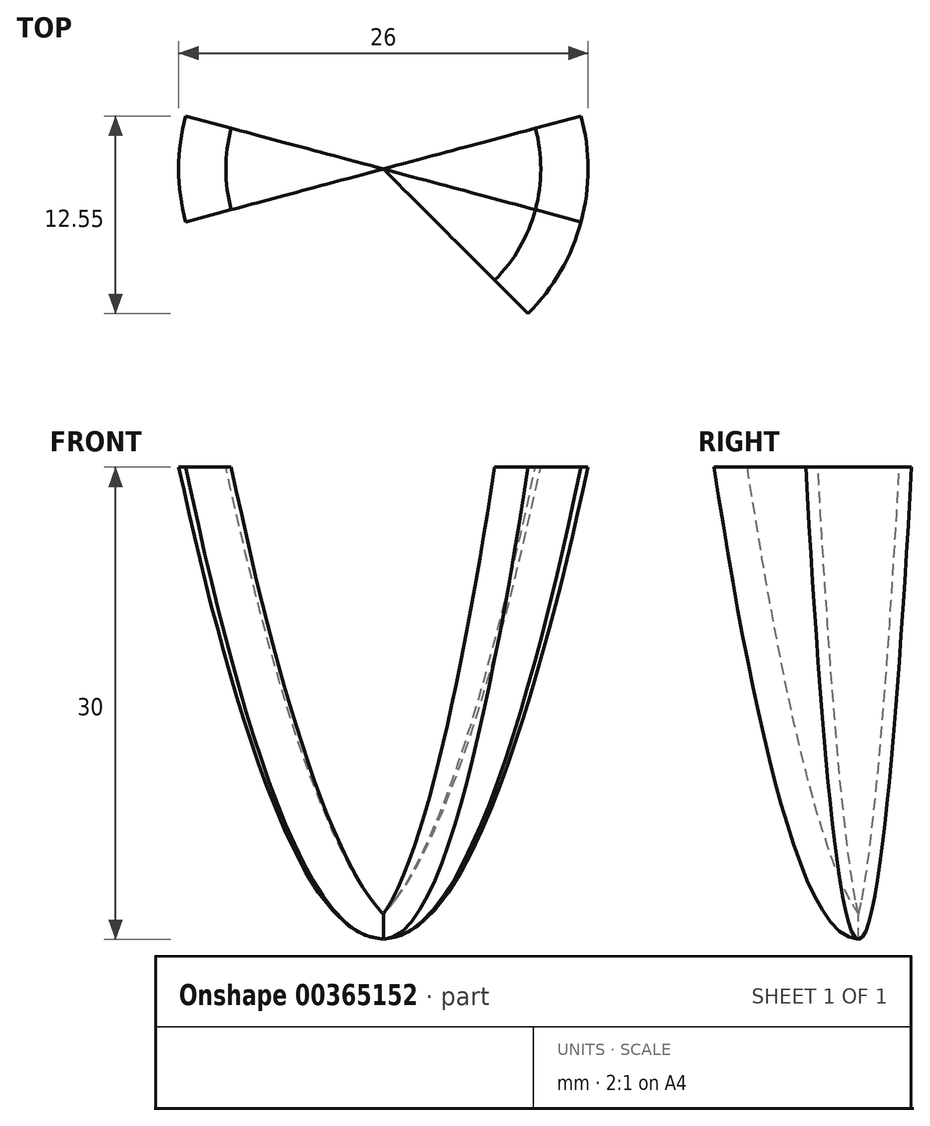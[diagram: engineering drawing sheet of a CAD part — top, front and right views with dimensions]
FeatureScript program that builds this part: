
annotation { "Feature Type Name" : "Feature", "Feature Type Description" : "" }
export const myFeature = defineFeature(function(context is Context, id is Id, definition is map)
    precondition{}
    {
        {
            var Q0;
            Q0=qCreatedBy(makeId("Front.planeOp"),FACE);
            var sketch = newSketch(context, id + "F0", { "sketchPlane" : qUnion([Q0])});
            skLineSegment(sketch, "E0", {"start": v(0, 0) * mm, "end": v(-13, 0) * mm});
            skLineSegment(sketch, "E1", {"start": v(-13, 0) * mm, "end": v(-13, -32) * mm, "construction": true});
            skLineSegment(sketch, "E2", {"start": v(-13, -32) * mm, "end": v(0, -32) * mm, "construction": true});
            skLineSegment(sketch, "E3.0", {"start": v(0, -2) * mm, "end": v(-13, -2) * mm});
            skLineSegment(sketch, "E4", {"start": v(0, 0) * mm, "end": v(-9, 0) * mm});
            skLineSegment(sketch, "E5", {"start": v(0, 0) * mm, "end": v(-3.25, 0) * mm});
            skLineSegment(sketch, "E6.MirrorCS", {"start": v(0, -2) * mm, "end": v(13, -2) * mm, "construction": true});
            skLineSegment(sketch, "E7.4", {"start": v(-5.38, 13) * mm, "end": v(5.38, 13) * mm});
            skPoint(sketch, "E7.0.midPoint", {"position": v(0, -32) * mm});
            skLineSegment(sketch, "E8.MirrorCS", {"start": v(13, 0) * mm, "end": v(13, -32) * mm, "construction": true});
            skLineSegment(sketch, "E9.MirrorCS", {"start": v(13, -32) * mm, "end": v(0, -32) * mm, "construction": true});
            skLineSegment(sketch, "E10.0", {"start": v(-8, 0) * mm, "end": v(-8, -32) * mm, "construction": true});
            skLineSegment(sketch, "E11.0", {"start": v(-12, 0) * mm, "end": v(-12, -32) * mm, "construction": true});
            skLineSegment(sketch, "E12.0", {"start": v(-11, 0) * mm, "end": v(-11, -32) * mm, "construction": true});
            skLineSegment(sketch, "E13.0", {"start": v(-10, 0) * mm, "end": v(-10, -32) * mm, "construction": true});
            skLineSegment(sketch, "E14.0", {"start": v(-9, 0) * mm, "end": v(-9, -32) * mm, "construction": true});
            skLineSegment(sketch, "E15.0", {"start": v(-3, 0) * mm, "end": v(-3, -32) * mm, "construction": true});
            skLineSegment(sketch, "E16.0", {"start": v(-4, 0) * mm, "end": v(-4, -32) * mm, "construction": true});
            skLineSegment(sketch, "E17.0", {"start": v(-5, 0) * mm, "end": v(-5, -32) * mm, "construction": true});
            skLineSegment(sketch, "E18.0", {"start": v(-6, 0) * mm, "end": v(-6, -32) * mm, "construction": true});
            skLineSegment(sketch, "E19.0", {"start": v(-7, 0) * mm, "end": v(-7, -32) * mm, "construction": true});
            skLineSegment(sketch, "E20.0", {"start": v(-2, 0) * mm, "end": v(-2, -32) * mm, "construction": true});
            skLineSegment(sketch, "E21.0", {"start": v(-1, 0) * mm, "end": v(-1, -32) * mm, "construction": true});
            skLineSegment(sketch, "E22.0", {"start": v(0, -116.4) * mm, "end": v(-13, -116.4) * mm, "construction": true});
            skLineSegment(sketch, "E23.0", {"start": v(0, -31.8) * mm, "end": v(-13, -31.8) * mm, "construction": true});
            skLineSegment(sketch, "E24.0", {"start": v(0, -31.3) * mm, "end": v(-13, -31.3) * mm, "construction": true});
            skLineSegment(sketch, "E25.0", {"start": v(0, -30.4) * mm, "end": v(-13, -30.4) * mm, "construction": true});
            skLineSegment(sketch, "E26.0", {"start": v(0, -29.2) * mm, "end": v(-13, -29.2) * mm, "construction": true});
            skLineSegment(sketch, "E27.0", {"start": v(0, -27.6) * mm, "end": v(-13, -27.6) * mm, "construction": true});
            skLineSegment(sketch, "E28.0", {"start": v(0, -25.6) * mm, "end": v(-13, -25.6) * mm, "construction": true});
            skLineSegment(sketch, "E29.0", {"start": v(0, -23.3) * mm, "end": v(-13, -23.3) * mm, "construction": true});
            skLineSegment(sketch, "E30.0", {"start": v(0, -20.6) * mm, "end": v(-13, -20.6) * mm, "construction": true});
            skLineSegment(sketch, "E31.0", {"start": v(0, -17.6) * mm, "end": v(-13, -17.6) * mm, "construction": true});
            skLineSegment(sketch, "E32.0", {"start": v(0, -14.2) * mm, "end": v(-13, -14.2) * mm, "construction": true});
            skLineSegment(sketch, "E33.0", {"start": v(0, -10.5) * mm, "end": v(-13, -10.5) * mm, "construction": true});
            skLineSegment(sketch, "E34.0", {"start": v(0, -6.4) * mm, "end": v(-13, -6.4) * mm, "construction": true});
            skFitSpline(sketch, "E35", {"points": [v(0, -32) * mm, v(-1, -31.8) * mm, v(-2, -31.3) * mm, v(-3, -30.4) * mm, v(-4, -29.2) * mm, v(-5, -27.6) * mm, v(-6, -25.6) * mm, v(-7, -23.3) * mm, v(-8, -20.6) * mm, v(-9, -17.6) * mm, v(-10, -14.2) * mm, v(-11, -10.5) * mm, v(-12, -6.4) * mm, v(-13, -2) * mm], "startDerivative": vector(-20.36, 2.94) * mm, "endDerivative": vector(-9.56, 42.59) * mm});
            skFitSpline(sketch, "E36", {"points": [v(0, -30.4) * mm, v(-1, -29.2) * mm, v(-2, -27.6) * mm, v(-3, -25.6) * mm, v(-4, -23.3) * mm, v(-5, -20.6) * mm, v(-6, -17.6) * mm, v(-7, -14.2) * mm, v(-8, -10.5) * mm, v(-9, -6.4) * mm, v(-10, -2) * mm], "startDerivative": vector(-14.02, 15.78) * mm, "endDerivative": vector(-8.05, 35.86) * mm});
            skArc(sketch, "E37.filletArc", {"start": v(-0.78, -29.48) * mm, "mid": v(-0.44, -29.76) * mm, "end": v(0, -29.86) * mm});
            skLineSegment(sketch, "E38", {"start": v(0, 0) * mm, "end": v(13, 0) * mm, "construction": true});
            skLineSegment(sketch, "E39", {"start": v(-13, -2) * mm, "end": v(-13, 0) * mm});
            skLineSegment(sketch, "E40", {"start": v(0, -32) * mm, "end": v(0, -29.86) * mm});
            skSolve(sketch);
        }
        {
            var Q0;
            {var subQ1=sQuery(id+"F0.wireOp",EDGE,"E35");Q0=makeQuery(id+"F0.imprint","IMPRINT",FACE,{"disambiguationData":[TD([[makeQuery(id+"F0.imprint","IMPRINT",EDGE,{"derivedFrom":subQ1}),-1.0]])]});}
            var Q1;
            Q1=sQuery(id+"F0.wireOp",EDGE,"E40");
            revolve(context, id + "F1", {"entities" : qUnion([Q0]), "axis" : qUnion([Q1]), "revolveType" : RevolveType.ONE_DIRECTION, "angle" : 15 * degree});
        }
        {
            var Q0;
            Q0=makeQuery(id+"F1.opRevolve","SWEPT_BODY",BODY,{"disambiguationData":[OSD([sQuery(id+"F0.wireOp",EDGE,"E3.0"),sQuery(id+"F0.wireOp",EDGE,"E35"),sQuery(id+"F0.wireOp",EDGE,"E36"),sQuery(id+"F0.wireOp",EDGE,"E37.filletArc"),sQuery(id+"F0.wireOp",EDGE,"E40")])]});
            var Q1;
            Q1=qCreatedBy(makeId("Right.planeOp"),FACE);
            mirror(context, id + "F2", {"entities" : qUnion([Q0]), "mirrorPlane" : qUnion([Q1])});
        }
        {
            var Q0;
            Q0=makeQuery(id+"F2.opPattern","COPY",BODY,{"derivedFrom":makeQuery(id+"F1.opRevolve","SWEPT_BODY",BODY,{"disambiguationData":[OSD([sQuery(id+"F0.wireOp",EDGE,"E3.0"),sQuery(id+"F0.wireOp",EDGE,"E35"),sQuery(id+"F0.wireOp",EDGE,"E36"),sQuery(id+"F0.wireOp",EDGE,"E37.filletArc"),sQuery(id+"F0.wireOp",EDGE,"E40")])]}),"instanceName":"1"});
            var Q1;
            Q1=makeQuery(id+"F2.opPattern","COPY",FACE,{"derivedFrom":makeQuery(id+"F1.opRevolve","CAP_FACE",FACE,{"disambiguationData":[OSD([sQuery(id+"F0.wireOp",EDGE,"E3.0"),sQuery(id+"F0.wireOp",EDGE,"E35"),sQuery(id+"F0.wireOp",EDGE,"E36"),sQuery(id+"F0.wireOp",EDGE,"E37.filletArc"),sQuery(id+"F0.wireOp",EDGE,"E40")])],"isStart":true}),"instanceName":"1"});
            mirror(context, id + "F3", {"operationType" : NewBodyOperationType.ADD, "entities" : qUnion([Q0]), "mirrorPlane" : qUnion([Q1])});
        }
        {
            var Q0;
            Q0=makeQuery(id+"F1.opRevolve","SWEPT_BODY",BODY,{"disambiguationData":[OSD([sQuery(id+"F0.wireOp",EDGE,"E3.0"),sQuery(id+"F0.wireOp",EDGE,"E35"),sQuery(id+"F0.wireOp",EDGE,"E36"),sQuery(id+"F0.wireOp",EDGE,"E37.filletArc"),sQuery(id+"F0.wireOp",EDGE,"E40")])]});
            var Q1;
            Q1=makeQuery(id+"F1.opRevolve","CAP_FACE",FACE,{"disambiguationData":[OSD([sQuery(id+"F0.wireOp",EDGE,"E3.0"),sQuery(id+"F0.wireOp",EDGE,"E35"),sQuery(id+"F0.wireOp",EDGE,"E36"),sQuery(id+"F0.wireOp",EDGE,"E37.filletArc"),sQuery(id+"F0.wireOp",EDGE,"E40")])],"isStart":true});
            mirror(context, id + "F4", {"operationType" : NewBodyOperationType.ADD, "entities" : qUnion([Q0]), "mirrorPlane" : qUnion([Q1])});
        }
        {
            var Q0;
            Q0=makeQuery(id+"F2.opPattern","COPY",BODY,{"derivedFrom":makeQuery(id+"F1.opRevolve","SWEPT_BODY",BODY,{"disambiguationData":[OSD([sQuery(id+"F0.wireOp",EDGE,"E3.0"),sQuery(id+"F0.wireOp",EDGE,"E35"),sQuery(id+"F0.wireOp",EDGE,"E36"),sQuery(id+"F0.wireOp",EDGE,"E37.filletArc"),sQuery(id+"F0.wireOp",EDGE,"E40")])]}),"instanceName":"1"});
            var Q1;
            Q1=makeQuery(id+"F2.opPattern","COPY",FACE,{"derivedFrom":makeQuery(id+"F1.opRevolve","CAP_FACE",FACE,{"disambiguationData":[OSD([sQuery(id+"F0.wireOp",EDGE,"E3.0"),sQuery(id+"F0.wireOp",EDGE,"E35"),sQuery(id+"F0.wireOp",EDGE,"E36"),sQuery(id+"F0.wireOp",EDGE,"E37.filletArc"),sQuery(id+"F0.wireOp",EDGE,"E40")])],"isStart":false}),"instanceName":"1"});
            mirror(context, id + "F5", {"operationType" : NewBodyOperationType.ADD, "entities" : qUnion([Q0]), "mirrorPlane" : qUnion([Q1])});
        }
    });
